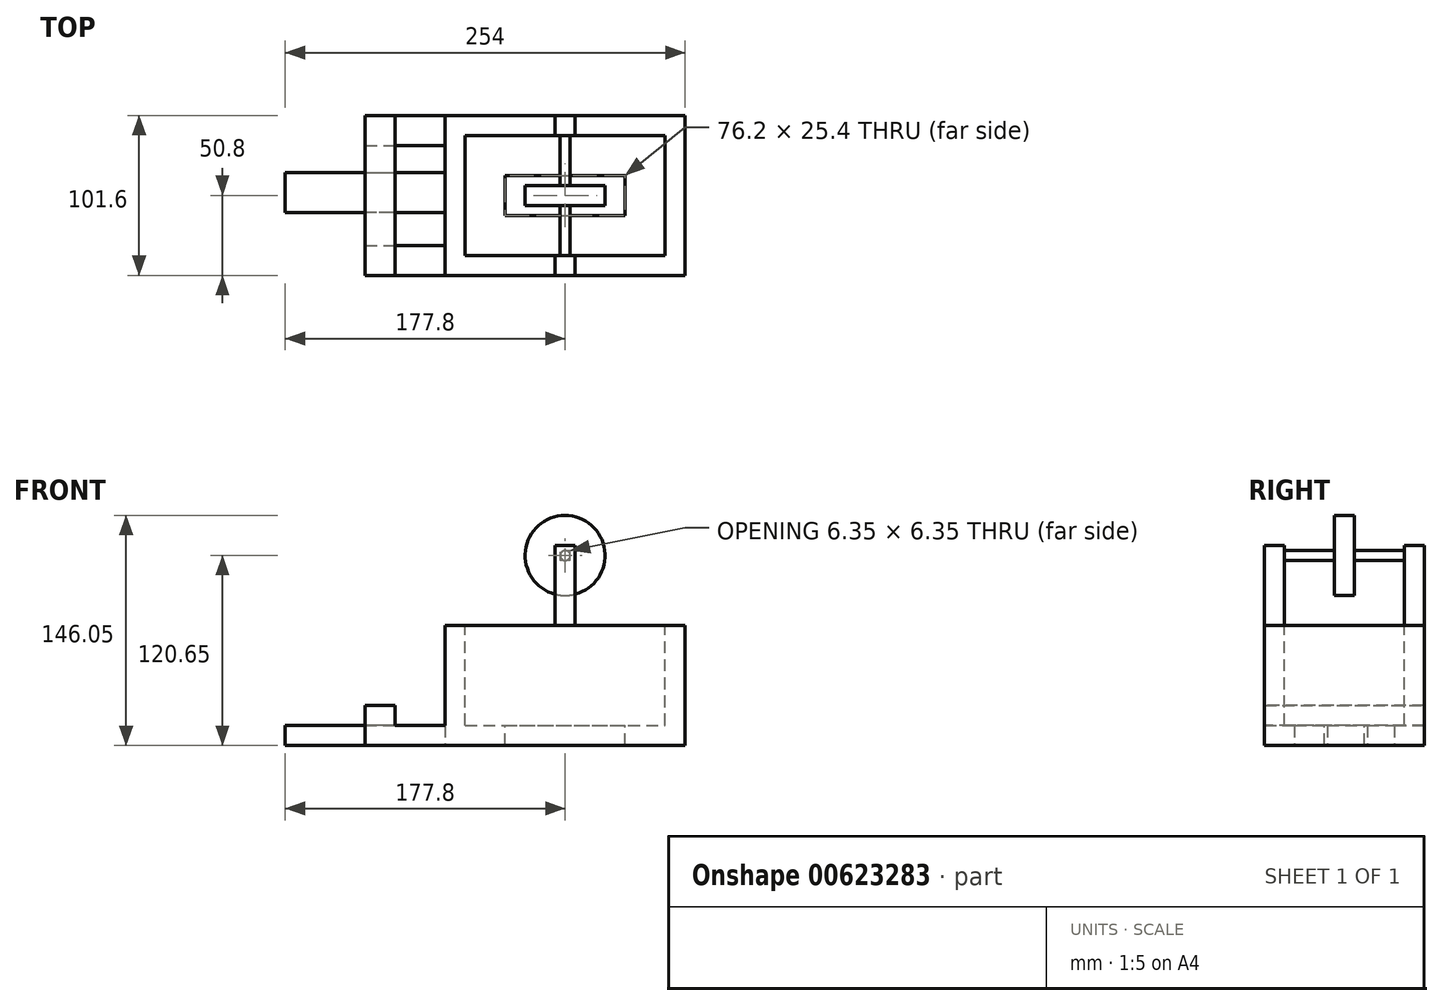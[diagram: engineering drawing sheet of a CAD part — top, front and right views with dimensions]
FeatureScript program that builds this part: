
annotation { "Feature Type Name" : "Feature", "Feature Type Description" : "" }
export const myFeature = defineFeature(function(context is Context, id is Id, definition is map)
    precondition{}
    {
        {
            var Q0;
            Q0=qCreatedBy(makeId("Front.planeOp"),FACE);
            var sketch = newSketch(context, id + "F0", { "sketchPlane" : qUnion([Q0])});
            skLineSegment(sketch, "E0.bottom", {"start": v(0, 0) * mm, "end": v(152.4, 0) * mm});
            skLineSegment(sketch, "E0.top", {"start": v(0, 76.2) * mm, "end": v(152.4, 76.2) * mm});
            skLineSegment(sketch, "E0.left", {"start": v(0, 0) * mm, "end": v(0, 76.2) * mm});
            skLineSegment(sketch, "E0.right", {"start": v(152.4, 0) * mm, "end": v(152.4, 76.2) * mm});
            skSolve(sketch);
        }
        {
            var Q0;
            Q0=makeQuery(id+"F0.imprint","IMPRINT",FACE,{"disambiguationData":[TD([[makeQuery(id+"F0.imprint","IMPRINT",EDGE,{"derivedFrom":sQuery(id+"F0.wireOp",EDGE,"E0.bottom")}),1.0]])]});
            extrude(context, id + "F1", {"entities" : qUnion([Q0]), "oppositeDirection" : true, "depth" : 101.6 * mm, "offsetDistance" : 25.4 * mm});
        }
        {
            var Q0;
            Q0=makeQuery(id+"F1.opExtrude","SWEPT_FACE",FACE,{"disambiguationData":[OSD([sQuery(id+"F0.wireOp",EDGE,"E0.top")])]});
            var sketch = newSketch(context, id + "F2", { "sketchPlane" : qUnion([Q0])});
            skLineSegment(sketch, "E1.bottom", {"start": v(12.7, 88.9) * mm, "end": v(139.7, 88.9) * mm});
            skLineSegment(sketch, "E1.top", {"start": v(12.7, 12.7) * mm, "end": v(139.7, 12.7) * mm});
            skLineSegment(sketch, "E1.left", {"start": v(12.7, 88.9) * mm, "end": v(12.7, 12.7) * mm});
            skLineSegment(sketch, "E1.right", {"start": v(139.7, 88.9) * mm, "end": v(139.7, 12.7) * mm});
            skSolve(sketch);
        }
        {
            var Q0;
            Q0=makeQuery(id+"F2.imprint","IMPRINT",FACE,{"disambiguationData":[TD([[makeQuery(id+"F2.imprint","IMPRINT",EDGE,{"derivedFrom":sQuery(id+"F2.wireOp",EDGE,"E1.bottom")}),-1.0]])]});
            extrude(context, id + "F3", {"entities" : qUnion([Q0]), "operationType" : NewBodyOperationType.REMOVE, "oppositeDirection" : true, "depth" : 63.5 * mm, "offsetDistance" : 25.4 * mm});
        }
        {
            var Q0;
            Q0=makeQuery(id+"F3.boolean.opBoolean","COPY",FACE,{"derivedFrom":makeQuery(id+"F3.opExtrude","CAP_FACE",FACE,{"disambiguationData":[OSD([sQuery(id+"F2.wireOp",EDGE,"E1.bottom"),sQuery(id+"F2.wireOp",EDGE,"E1.top"),sQuery(id+"F2.wireOp",EDGE,"E1.left"),sQuery(id+"F2.wireOp",EDGE,"E1.right")])],"isStart":false})});
            var sketch = newSketch(context, id + "F4", { "sketchPlane" : qUnion([Q0])});
            skLineSegment(sketch, "E2.bottom", {"start": v(38.1, 63.5) * mm, "end": v(114.3, 63.5) * mm});
            skLineSegment(sketch, "E2.top", {"start": v(38.1, 38.1) * mm, "end": v(114.3, 38.1) * mm});
            skLineSegment(sketch, "E2.left", {"start": v(38.1, 63.5) * mm, "end": v(38.1, 38.1) * mm});
            skLineSegment(sketch, "E2.right", {"start": v(114.3, 63.5) * mm, "end": v(114.3, 38.1) * mm});
            skSolve(sketch);
        }
        {
            var Q0;
            Q0=makeQuery(id+"F4.imprint","IMPRINT",FACE,{"disambiguationData":[TD([[makeQuery(id+"F4.imprint","IMPRINT",EDGE,{"derivedFrom":sQuery(id+"F4.wireOp",EDGE,"E2.bottom")}),-1.0]])]});
            extrude(context, id + "F5", {"entities" : qUnion([Q0]), "operationType" : NewBodyOperationType.REMOVE, "oppositeDirection" : true, "depth" : 12.7 * mm, "offsetDistance" : 25.4 * mm});
        }
        {
            var Q0;
            Q0=makeQuery(id+"F1.opExtrude","SWEPT_FACE",FACE,{"disambiguationData":[OSD([sQuery(id+"F0.wireOp",EDGE,"E0.top")])]});
            var sketch = newSketch(context, id + "F6", { "sketchPlane" : qUnion([Q0])});
            skLineSegment(sketch, "E3.bottom", {"start": v(69.85, 101.6) * mm, "end": v(82.55, 101.6) * mm});
            skLineSegment(sketch, "E3.top", {"start": v(69.85, 88.9) * mm, "end": v(82.55, 88.9) * mm});
            skLineSegment(sketch, "E3.left", {"start": v(69.85, 101.6) * mm, "end": v(69.85, 88.9) * mm});
            skLineSegment(sketch, "E3.right", {"start": v(82.55, 101.6) * mm, "end": v(82.55, 88.9) * mm});
            skSolve(sketch);
        }
        {
            var Q0;
            Q0=makeQuery(id+"F6.imprint","IMPRINT",FACE,{"disambiguationData":[TD([[makeQuery(id+"F6.imprint","IMPRINT",EDGE,{"derivedFrom":sQuery(id+"F6.wireOp",EDGE,"E3.bottom")}),-1.0]])]});
            extrude(context, id + "F7", {"entities" : qUnion([Q0]), "depth" : 50.8 * mm, "offsetDistance" : 25.4 * mm});
        }
        {
            var Q0;
            Q0=makeQuery(id+"F1.opExtrude","SWEPT_FACE",FACE,{"disambiguationData":[OSD([sQuery(id+"F0.wireOp",EDGE,"E0.top")])]});
            var sketch = newSketch(context, id + "F8", { "sketchPlane" : qUnion([Q0])});
            skLineSegment(sketch, "E4.bottom", {"start": v(69.85, 12.7) * mm, "end": v(82.55, 12.7) * mm});
            skLineSegment(sketch, "E4.top", {"start": v(69.85, 0) * mm, "end": v(82.55, 0) * mm});
            skLineSegment(sketch, "E4.left", {"start": v(69.85, 12.7) * mm, "end": v(69.85, 0) * mm});
            skLineSegment(sketch, "E4.right", {"start": v(82.55, 12.7) * mm, "end": v(82.55, 0) * mm});
            skSolve(sketch);
        }
        {
            var Q0;
            Q0=makeQuery(id+"F8.imprint","IMPRINT",FACE,{"disambiguationData":[TD([[makeQuery(id+"F8.imprint","IMPRINT",EDGE,{"derivedFrom":sQuery(id+"F8.wireOp",EDGE,"E4.bottom")}),-1.0]])]});
            extrude(context, id + "F9", {"entities" : qUnion([Q0]), "depth" : 50.8 * mm, "offsetDistance" : 25.4 * mm});
        }
        {
            var Q0;
            Q0=makeQuery(id+"F9.boolean.opBoolean","MERGE",FACE,{"derivedFrom":[makeQuery(id+"F1.opExtrude","CAP_FACE",FACE,{"disambiguationData":[OSD([sQuery(id+"F0.wireOp",EDGE,"E0.bottom"),sQuery(id+"F0.wireOp",EDGE,"E0.top"),sQuery(id+"F0.wireOp",EDGE,"E0.left"),sQuery(id+"F0.wireOp",EDGE,"E0.right")])],"isStart":true}),makeQuery(id+"F9.opExtrude","SWEPT_FACE",FACE,{"disambiguationData":[OSD([sQuery(id+"F8.wireOp",EDGE,"E4.top")])]})]});
            var sketch = newSketch(context, id + "F10", { "sketchPlane" : qUnion([Q0])});
            skCircle(sketch, "E5", {"center": v(76.2, 120.65) * mm, "radius": 3.18 * mm});
            skSolve(sketch);
        }
        {
            var Q0;
            Q0=makeQuery(id+"F10.imprint","IMPRINT",FACE,{"disambiguationData":[TD([[makeQuery(id+"F10.imprint","IMPRINT",EDGE,{"derivedFrom":sQuery(id+"F10.wireOp",EDGE,"E5")}),1.0]])]});
            extrude(context, id + "F11", {"entities" : qUnion([Q0]), "operationType" : NewBodyOperationType.ADD, "oppositeDirection" : true, "depth" : 101.6 * mm, "offsetDistance" : 25.4 * mm});
        }
        {
            var Q0;
            Q0=qCreatedBy(makeId("Front.planeOp"),FACE);
            cPlane(context, id + "F12", {"entities" : qUnion([Q0]), "cplaneType" : CPlaneType.OFFSET, "offset" : 50.8 * mm, "oppositeDirection" : true, "width" : 152.4 * mm, "height" : 152.4 * mm});
        }
        {
            var Q0;
            Q0=qCreatedBy(id+"F12.planeOp",FACE);
            var sketch = newSketch(context, id + "F13", { "sketchPlane" : qUnion([Q0])});
            skCircle(sketch, "E6", {"center": v(76.1, 120.65) * mm, "radius": 25.4 * mm});
            skSolve(sketch);
        }
        {
            var Q0;
            Q0=makeQuery(id+"F13.imprint","IMPRINT",FACE,{"disambiguationData":[TD([[makeQuery(id+"F13.imprint","IMPRINT",EDGE,{"derivedFrom":sQuery(id+"F13.wireOp",EDGE,"E6")}),1.0]])]});
            extrude(context, id + "F14", {"entities" : qUnion([Q0]), "operationType" : NewBodyOperationType.ADD, "endBound" : BoundingType.SYMMETRIC, "depth" : 12.7 * mm, "offsetDistance" : 25.4 * mm});
        }
        {
            var Q0;
            Q0=makeQuery(id+"F1.opExtrude","SWEPT_FACE",FACE,{"disambiguationData":[OSD([sQuery(id+"F0.wireOp",EDGE,"E0.bottom")])]});
            var sketch = newSketch(context, id + "F15", { "sketchPlane" : qUnion([Q0])});
            skLineSegment(sketch, "E7", {"start": v(0, -50.8) * mm, "end": v(0, -39.8) * mm});
            skLineSegment(sketch, "E8", {"start": v(0, -39.8) * mm, "end": v(0, -65.2) * mm});
            skLineSegment(sketch, "E9", {"start": v(0, -39.8) * mm, "end": v(-101.6, -39.8) * mm});
            skLineSegment(sketch, "E10", {"start": v(-101.6, -39.8) * mm, "end": v(-101.6, -65.2) * mm});
            skLineSegment(sketch, "E11", {"start": v(-101.6, -65.2) * mm, "end": v(0, -65.2) * mm});
            skSolve(sketch);
        }
        {
            var Q0;
            {var subQ0=sQuery(id+"F15.wireOp",EDGE,"E9");Q0=makeQuery(id+"F15.imprint","IMPRINT",FACE,{"disambiguationData":[TD([[makeQuery(id+"F15.imprint","IMPRINT",EDGE,{"derivedFrom":subQ0}),1.0]])]});}
            extrude(context, id + "F16", {"entities" : qUnion([Q0]), "operationType" : NewBodyOperationType.ADD, "oppositeDirection" : true, "depth" : 12.7 * mm, "offsetDistance" : 25.4 * mm});
        }
        {
            var Q0;
            Q0=makeQuery(id+"F16.boolean.opBoolean","MERGE",FACE,{"derivedFrom":[makeQuery(id+"F1.opExtrude","SWEPT_FACE",FACE,{"disambiguationData":[OSD([sQuery(id+"F0.wireOp",EDGE,"E0.bottom")])]}),makeQuery(id+"F16.opExtrude","CAP_FACE",FACE,{"disambiguationData":[OSD([sQuery(id+"F15.wireOp",EDGE,"E8"),sQuery(id+"F15.wireOp",EDGE,"E9"),sQuery(id+"F15.wireOp",EDGE,"E10"),sQuery(id+"F15.wireOp",EDGE,"E11")])],"isStart":true})]});
            var sketch = newSketch(context, id + "F17", { "sketchPlane" : qUnion([Q0])});
            skLineSegment(sketch, "E12", {"start": v(0, 0) * mm, "end": v(-50.8, 0) * mm});
            skLineSegment(sketch, "E13", {"start": v(-50.8, 0) * mm, "end": v(-50.8, -19.05) * mm});
            skLineSegment(sketch, "E14", {"start": v(-50.8, -19.05) * mm, "end": v(0, -19.05) * mm});
            skSolve(sketch);
        }
        {
            var Q0;
            {var subQ5=sQuery(id+"F0.wireOp",EDGE,"E0.bottom");var subQ6=makeQuery(id+"F1.opExtrude","CAP_EDGE",EDGE,{"disambiguationData":[OSD([subQ5])],"isStart":true});Q0=makeQuery(id+"F17.imprint","IMPRINT",FACE,{"disambiguationData":[TD([[makeQuery(id+"F17.imprint","IMPRINT",EDGE,{"derivedFrom":subQ6}),-1.0]])]});}
            var sketch = newSketch(context, id + "F18", { "sketchPlane" : qUnion([Q0])});
            skSolve(sketch);
        }
        {
            var Q0;
            {var subQ0=sQuery(id+"F17.wireOp",EDGE,"E12");Q0=makeQuery(id+"F17.imprint","IMPRINT",FACE,{"disambiguationData":[TD([[makeQuery(id+"F17.imprint","IMPRINT",EDGE,{"derivedFrom":subQ0}),1.0]])]});}
            extrude(context, id + "F19", {"entities" : qUnion([Q0]), "operationType" : NewBodyOperationType.ADD, "oppositeDirection" : true, "depth" : 12.7 * mm, "offsetDistance" : 25.4 * mm});
        }
        {
            var Q0;
            {var subQ5=sQuery(id+"F0.wireOp",EDGE,"E0.bottom");var subQ6=makeQuery(id+"F1.opExtrude","CAP_EDGE",EDGE,{"disambiguationData":[OSD([subQ5])],"isStart":true});Q0=makeQuery(id+"F18.imprint","IMPRINT",FACE,{"disambiguationData":[TD([[makeQuery(id+"F18.imprint","IMPRINT",EDGE,{"derivedFrom":makeQuery(id+"F17.imprint","IMPRINT",EDGE,{"derivedFrom":subQ6})}),-1.0]])]});}
            var sketch = newSketch(context, id + "F20", { "sketchPlane" : qUnion([Q0])});
            skLineSegment(sketch, "E15", {"start": v(0, -101.51) * mm, "end": v(-50.8, -101.51) * mm});
            skLineSegment(sketch, "E16", {"start": v(-50.8, -101.51) * mm, "end": v(-50.8, -82.46) * mm});
            skLineSegment(sketch, "E17", {"start": v(-50.8, -82.46) * mm, "end": v(0, -82.46) * mm});
            skSolve(sketch);
        }
        {
            var Q0;
            {var subQ0=sQuery(id+"F20.wireOp",EDGE,"E15");Q0=makeQuery(id+"F20.imprint","IMPRINT",FACE,{"disambiguationData":[TD([[makeQuery(id+"F20.imprint","IMPRINT",EDGE,{"derivedFrom":subQ0}),-1.0]])]});}
            extrude(context, id + "F21", {"entities" : qUnion([Q0]), "operationType" : NewBodyOperationType.ADD, "oppositeDirection" : true, "depth" : 12.7 * mm, "offsetDistance" : 25.4 * mm});
        }
        {
            var Q0;
            Q0=makeQuery(id+"F16.opExtrude","CAP_FACE",FACE,{"disambiguationData":[OSD([sQuery(id+"F15.wireOp",EDGE,"E8"),sQuery(id+"F15.wireOp",EDGE,"E9"),sQuery(id+"F15.wireOp",EDGE,"E10"),sQuery(id+"F15.wireOp",EDGE,"E11")])],"isStart":false});
            var sketch = newSketch(context, id + "F22", { "sketchPlane" : qUnion([Q0])});
            skLineSegment(sketch, "E18", {"start": v(-51.05, 101.43) * mm, "end": v(-51.05, 0) * mm});
            skLineSegment(sketch, "E19", {"start": v(-51.05, 0) * mm, "end": v(-32, 0) * mm});
            skLineSegment(sketch, "E20", {"start": v(-32, 0) * mm, "end": v(-32, 101.54) * mm});
            skLineSegment(sketch, "E21", {"start": v(-32, 101.54) * mm, "end": v(-51.05, 101.43) * mm});
            skSolve(sketch);
        }
        {
            var Q0;
            {var subQ0=sQuery(id+"F22.wireOp",EDGE,"E21");Q0=makeQuery(id+"F22.imprint","IMPRINT",FACE,{"disambiguationData":[TD([[makeQuery(id+"F22.imprint","IMPRINT",EDGE,{"derivedFrom":subQ0}),1.0]])]});}
            var Q1;
            {var subQ0=sQuery(id+"F22.wireOp",EDGE,"E18");var subQ1=makeQuery(id+"F16.opExtrude","CAP_EDGE",EDGE,{"disambiguationData":[OSD([sQuery(id+"F15.wireOp",EDGE,"E11")])],"isStart":false});var subQ2=makeQuery(id+"F22.imprint","INTERSECT",VERTEX,{"derivedFrom":[subQ1,subQ0]});Q1=makeQuery(id+"F22.imprint","IMPRINT",FACE,{"disambiguationData":[TD([[makeQuery(id+"F22.imprint","IMPRINT",EDGE,{"disambiguationData":[TD([[subQ2,-1.0]])],"derivedFrom":subQ0}),1.0]])]});}
            var Q2;
            {var subQ0=sQuery(id+"F22.wireOp",EDGE,"E19");Q2=makeQuery(id+"F22.imprint","IMPRINT",FACE,{"disambiguationData":[TD([[makeQuery(id+"F22.imprint","IMPRINT",EDGE,{"derivedFrom":subQ0}),1.0]])]});}
            extrude(context, id + "F23", {"entities" : qUnion([Q0, Q1, Q2]), "operationType" : NewBodyOperationType.ADD, "depth" : 12.7 * mm, "offsetDistance" : 25.4 * mm});
        }
    });
